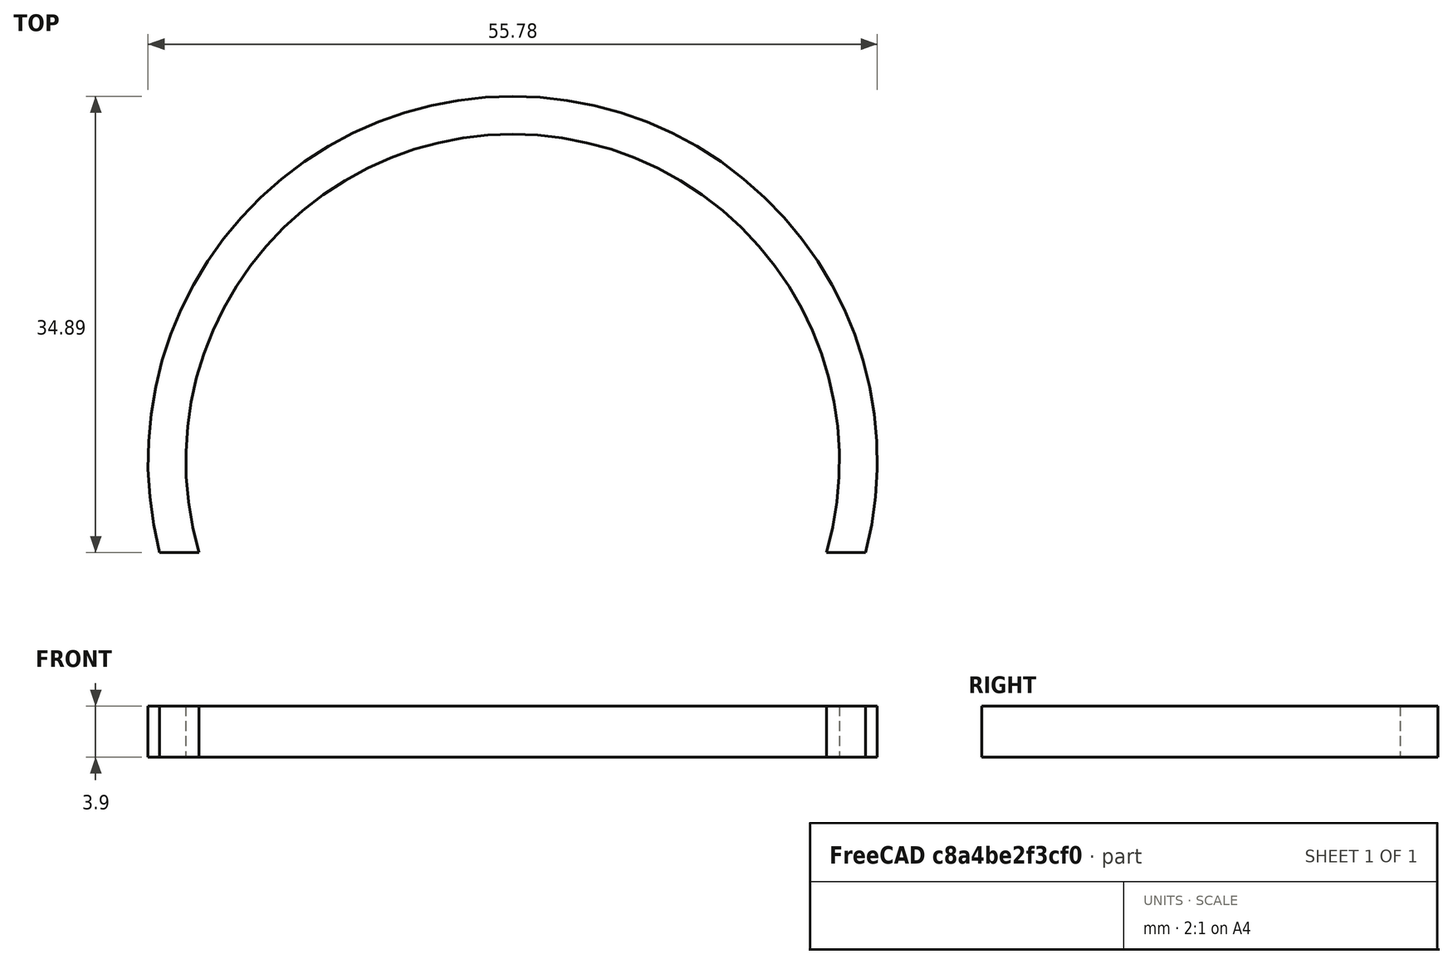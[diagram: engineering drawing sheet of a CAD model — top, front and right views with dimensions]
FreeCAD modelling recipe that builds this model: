
FCSTD DOCUMENT  (FreeCAD 0.19R22756 (Git))
Label: enta-locker-fixer
License: All rights reserved
LicenseURL: http://en.wikipedia.org/wiki/All_rights_reserved
objects: Sketcher::SketchObject×1, PartDesign::Pad×1, PartDesign::Body×1
note: 4 computed .brp shape members not serialized (recipe doc carries the construction recipe); baked Part::Feature solids carry a one-line shape summary decoded from their .brp

FEATURE [Sketcher::SketchObject] Sketch
  MapMode = 5
  Support = -> [XY_Plane]
  sketch-geometry (4):
    g0: ArcOfCircle CenterX=0 CenterY=0 CenterZ=0 NormalX=0 NormalY=0 NormalZ=1 AngleXU=0 Radius=25 StartAngle=5.99939 EndAngle=9.70857
    g1: LineSegment StartX=-24 StartY=-7 StartZ=0 EndX=-27 EndY=-7 EndZ=0
    g2: LineSegment StartX=24 StartY=-7 StartZ=0 EndX=27 EndY=-7 EndZ=0
    g3: ArcOfCircle CenterX=0 CenterY=0 CenterZ=0 NormalX=0 NormalY=0 NormalZ=1 AngleXU=0 Radius=27.8927 StartAngle=6.02951 EndAngle=9.67845
  constraints (12):
    c: Coincident(g0,g-1)
    c: Horizontal(g0,g0)
    c: Radius(g0) = 25
    c: DistanceY(g-1,g0) = -7
    c: Coincident(g1,g0)
    c: Horizontal(g1)
    c: Coincident(g2,g0)
    c: Equal(g1,g2)
    c: Coincident(g3,g0)
    c: Coincident(g3,g1)
    c: Coincident(g3,g2)
    c: Distance(g1) = 3
FEATURE [PartDesign::Pad] Pad
  Direction = (1,1,1)
  Length = 3.9
  Length2 = 100
  Profile = -> Sketch
  Type = 0
FEATURE [PartDesign::Body] Body
  Group = -> [Sketch,Pad]
  Origin = -> Origin
  Tip = -> Pad
